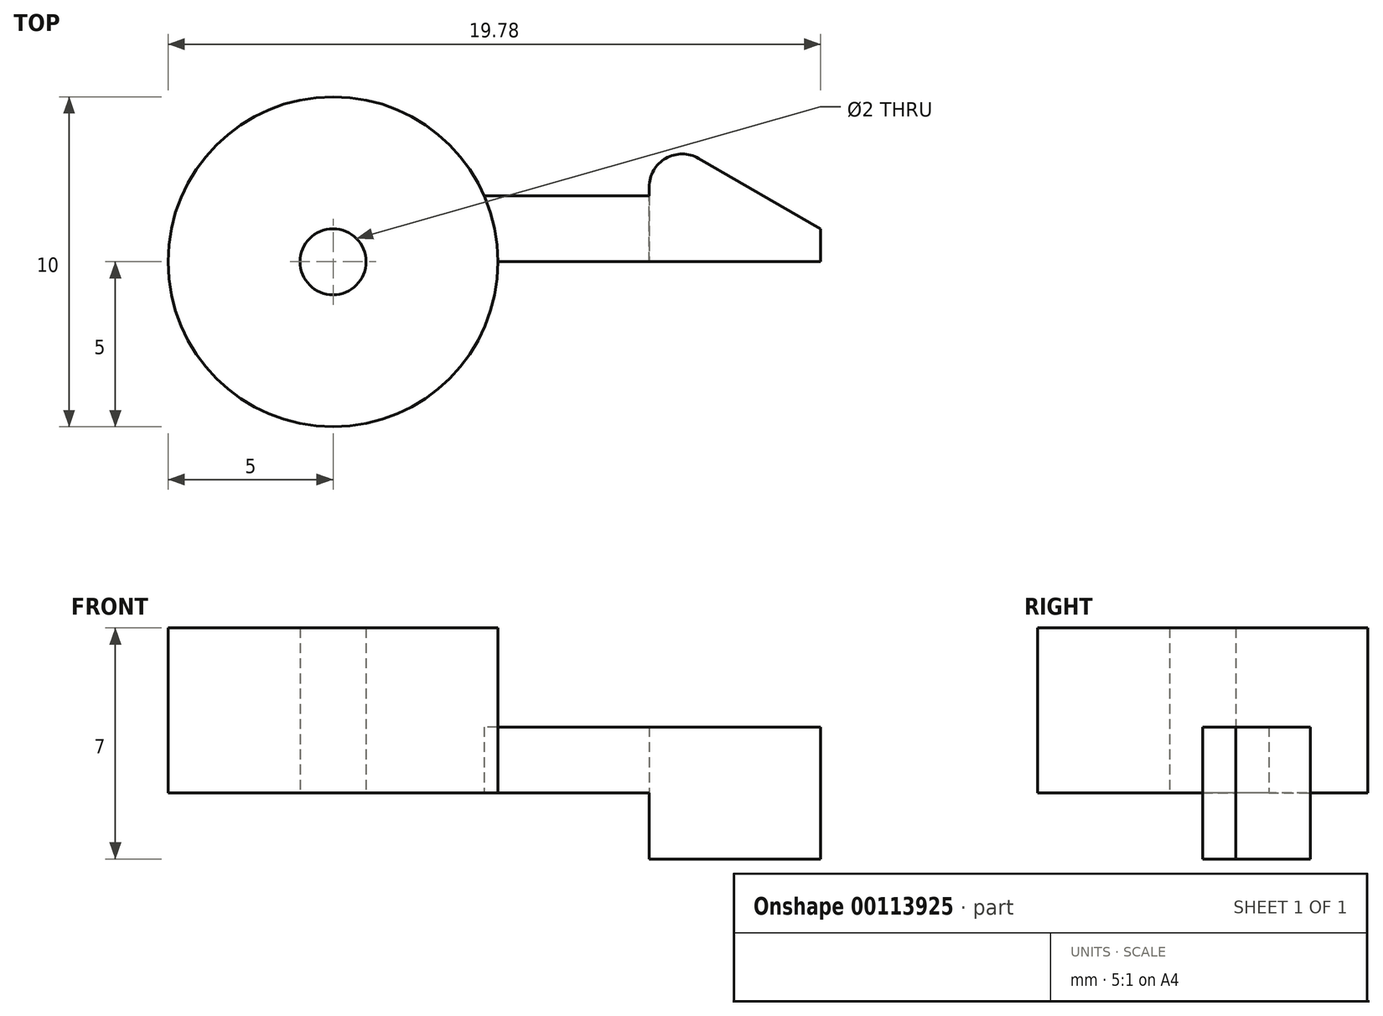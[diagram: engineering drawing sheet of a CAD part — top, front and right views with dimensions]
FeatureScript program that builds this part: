
annotation { "Feature Type Name" : "Feature", "Feature Type Description" : "" }
export const myFeature = defineFeature(function(context is Context, id is Id, definition is map)
    precondition{}
    {
        {
            var Q0;
            Q0=qCreatedBy(makeId("Top.planeOp"),FACE);
            var sketch = newSketch(context, id + "F0", { "sketchPlane" : qUnion([Q0])});
            skCircle(sketch, "E0", {"center": v(0, 0) * mm, "radius": 5 * mm});
            skLineSegment(sketch, "E1", {"start": v(5, 0) * mm, "end": v(9.58, 0) * mm});
            skLineSegment(sketch, "E2", {"start": v(9.58, 2) * mm, "end": v(9.58, 0) * mm});
            skLineSegment(sketch, "E3", {"start": v(9.58, 2) * mm, "end": v(4.58, 2) * mm});
            skLineSegment(sketch, "E4", {"start": v(9.58, 2) * mm, "end": v(9.58, 4) * mm});
            skLineSegment(sketch, "E5", {"start": v(9.58, 4) * mm, "end": v(14.78, 1) * mm});
            skLineSegment(sketch, "E6", {"start": v(14.78, 1) * mm, "end": v(14.78, 0) * mm});
            skLineSegment(sketch, "E7", {"start": v(14.78, 0) * mm, "end": v(9.58, 0) * mm});
            skSolve(sketch);
        }
        {
            var Q0;
            {var subQ0=sQuery(id+"F0.wireOp",EDGE,"E0");var subQ1=makeQuery(id+"F0.imprint","INTERSECT",VERTEX,{"derivedFrom":[subQ0,sQuery(id+"F0.wireOp",EDGE,"E1")]});Q0=makeQuery(id+"F0.imprint","IMPRINT",FACE,{"disambiguationData":[TD([[makeQuery(id+"F0.imprint","IMPRINT",EDGE,{"disambiguationData":[TD([[subQ1,-1.0]])],"derivedFrom":subQ0}),1.0]])]});}
            extrude(context, id + "F1", {"entities" : qUnion([Q0]), "depth" : 5 * mm});
        }
        {
            var Q0;
            {var subQ0=sQuery(id+"F0.wireOp",EDGE,"E1");Q0=makeQuery(id+"F0.imprint","IMPRINT",FACE,{"disambiguationData":[TD([[makeQuery(id+"F0.imprint","IMPRINT",EDGE,{"derivedFrom":subQ0}),1.0]])]});}
            extrude(context, id + "F2", {"entities" : qUnion([Q0]), "operationType" : NewBodyOperationType.ADD, "depth" : 2 * mm});
        }
        {
            var Q0;
            Q0=makeQuery(id+"F0.imprint","IMPRINT",FACE,{"disambiguationData":[TD([[makeQuery(id+"F0.imprint","IMPRINT",EDGE,{"derivedFrom":sQuery(id+"F0.wireOp",EDGE,"E2")}),1.0]])]});
            extrude(context, id + "F3", {"entities" : qUnion([Q0]), "operationType" : NewBodyOperationType.ADD, "endBound" : BoundingType.SYMMETRIC, "depth" : 4 * mm});
        }
        {
            var Q0;
            Q0=sQuery(id+"F0.wireOp",VERTEX,"E0.center");
            var Q1;
            Q1=makeQuery(id+"F1.opExtrude","SWEPT_BODY",BODY,{"disambiguationData":[OSD([sQuery(id+"F0.wireOp",EDGE,"E0")])]});
            hole(context, id + "F4", {"style" : HoleStyle.SIMPLE, "endStyle" : HoleEndStyle.THROUGH, "oppositeDirection" : true, "holeDiameter" : 2 * mm, "locations" : qUnion([Q0]), "scope" : qUnion([Q1]), "isTappedThrough" : true});
        }
        {
            var Q0;
            Q0=makeQuery(id+"F3.opExtrude","SWEPT_EDGE",EDGE,{"disambiguationData":[OSD([sQuery(id+"F0.wireOp",EDGE,"E4"),sQuery(id+"F0.wireOp",EDGE,"E5")])]});
            fillet(context, id + "F5", {"entities" : qUnion([Q0]), "radius" : 1 * mm, "tangentPropagation" : true, "allowEdgeOverflow" : false});
        }
    });
